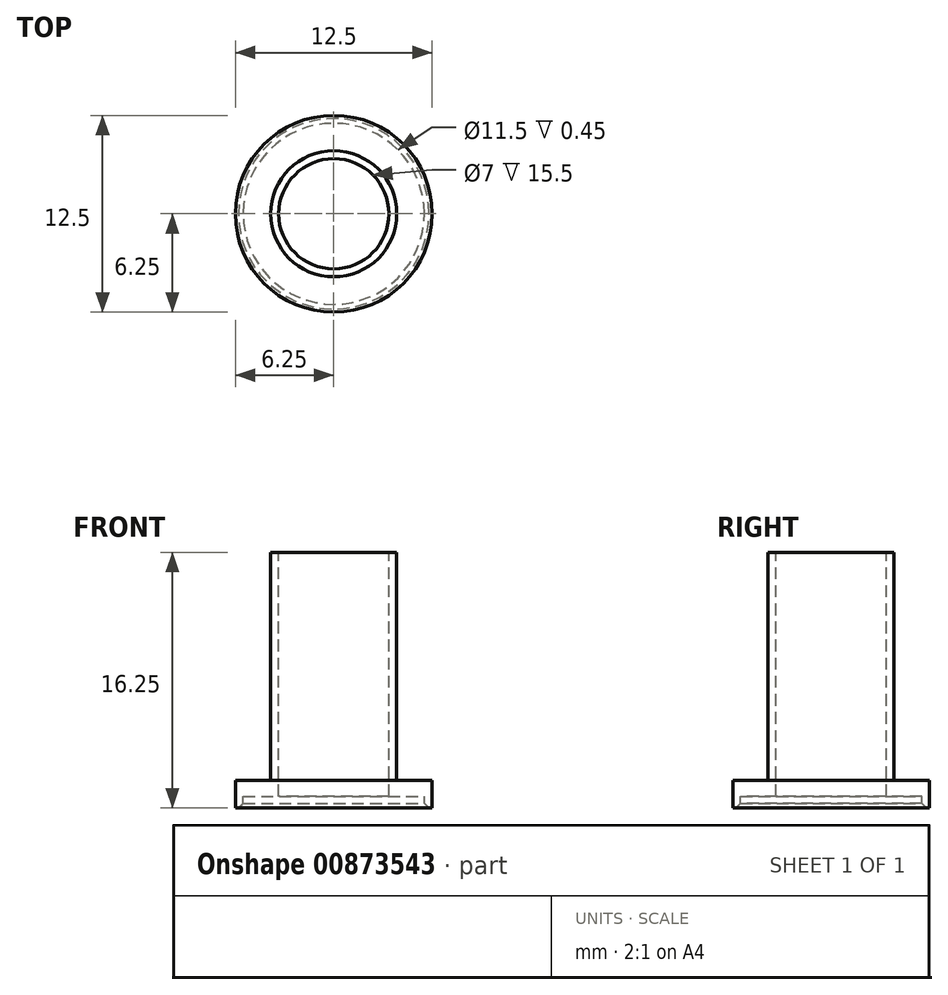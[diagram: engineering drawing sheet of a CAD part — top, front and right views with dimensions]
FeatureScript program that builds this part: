
annotation { "Feature Type Name" : "Feature", "Feature Type Description" : "" }
export const myFeature = defineFeature(function(context is Context, id is Id, definition is map)
    precondition{}
    {
        {
            var Q0;
            Q0=qCreatedBy(makeId("Top.planeOp"),FACE);
            var sketch = newSketch(context, id + "F0", { "sketchPlane" : qUnion([Q0])});
            skCircle(sketch, "E0", {"center": v(0, 0) * mm, "radius": 6.25 * mm});
            skSolve(sketch);
        }
        {
            var Q0;
            Q0=makeQuery(id+"F0.imprint","IMPRINT",FACE,{"disambiguationData":[TD([[makeQuery(id+"F0.imprint","IMPRINT",EDGE,{"derivedFrom":sQuery(id+"F0.wireOp",EDGE,"E0")}),1.0]])]});
            extrude(context, id + "F1", {"entities" : qUnion([Q0]), "depth" : 1 * mm, "offsetDistance" : 25 * mm});
        }
        {
            var Q0;
            Q0=makeQuery(id+"F1.opExtrude","CAP_FACE",FACE,{"disambiguationData":[OSD([sQuery(id+"F0.wireOp",EDGE,"E0")])],"isStart":true});
            var sketch = newSketch(context, id + "F2", { "sketchPlane" : qUnion([Q0])});
            skCircle(sketch, "E1", {"center": v(0, 0) * mm, "radius": 5.75 * mm});
            skSolve(sketch);
        }
        {
            var Q0;
            Q0=makeQuery(id+"F2.imprint","IMPRINT",FACE,{"disambiguationData":[TD([[makeQuery(id+"F2.imprint","IMPRINT",EDGE,{"derivedFrom":sQuery(id+"F2.wireOp",EDGE,"E1")}),-1.0]])]});
            extrude(context, id + "F3", {"entities" : qUnion([Q0]), "operationType" : NewBodyOperationType.ADD, "depth" : 0.75 * mm, "offsetDistance" : 25 * mm});
        }
        {
            var Q0;
            Q0=makeQuery(id+"F1.opExtrude","CAP_FACE",FACE,{"disambiguationData":[OSD([sQuery(id+"F0.wireOp",EDGE,"E0")])],"isStart":false});
            var sketch = newSketch(context, id + "F4", { "sketchPlane" : qUnion([Q0])});
            skCircle(sketch, "E2", {"center": v(0, 0) * mm, "radius": 4 * mm});
            skSolve(sketch);
        }
        {
            var Q0;
            Q0=makeQuery(id+"F4.imprint","IMPRINT",FACE,{"disambiguationData":[TD([[makeQuery(id+"F4.imprint","IMPRINT",EDGE,{"derivedFrom":sQuery(id+"F4.wireOp",EDGE,"E2")}),1.0]])]});
            extrude(context, id + "F5", {"entities" : qUnion([Q0]), "operationType" : NewBodyOperationType.ADD, "depth" : 14.5 * mm, "offsetDistance" : 25 * mm});
        }
        {
            var Q0;
            Q0=makeQuery(id+"F5.opExtrude","CAP_FACE",FACE,{"disambiguationData":[OSD([sQuery(id+"F4.wireOp",EDGE,"E2")])],"isStart":false});
            var sketch = newSketch(context, id + "F6", { "sketchPlane" : qUnion([Q0])});
            skCircle(sketch, "E3", {"center": v(0, 0) * mm, "radius": 3.5 * mm});
            skSolve(sketch);
        }
        {
            var Q0;
            Q0=makeQuery(id+"F6.imprint","IMPRINT",FACE,{"disambiguationData":[TD([[makeQuery(id+"F6.imprint","IMPRINT",EDGE,{"derivedFrom":sQuery(id+"F6.wireOp",EDGE,"E3")}),1.0]])]});
            extrude(context, id + "F7", {"entities" : qUnion([Q0]), "operationType" : NewBodyOperationType.REMOVE, "oppositeDirection" : true, "depth" : 25 * mm, "offsetDistance" : 25 * mm});
        }
        {
            var Q0;
            Q0=makeQuery(id+"F3.opExtrude","CAP_EDGE",EDGE,{"disambiguationData":[OSD([sQuery(id+"F2.wireOp",EDGE,"E1")])],"isStart":false});
            chamfer(context, id + "F8", {"entities" : qUnion([Q0]), "width" : 0.3 * mm, "tangentPropagation" : true});
        }
    });
